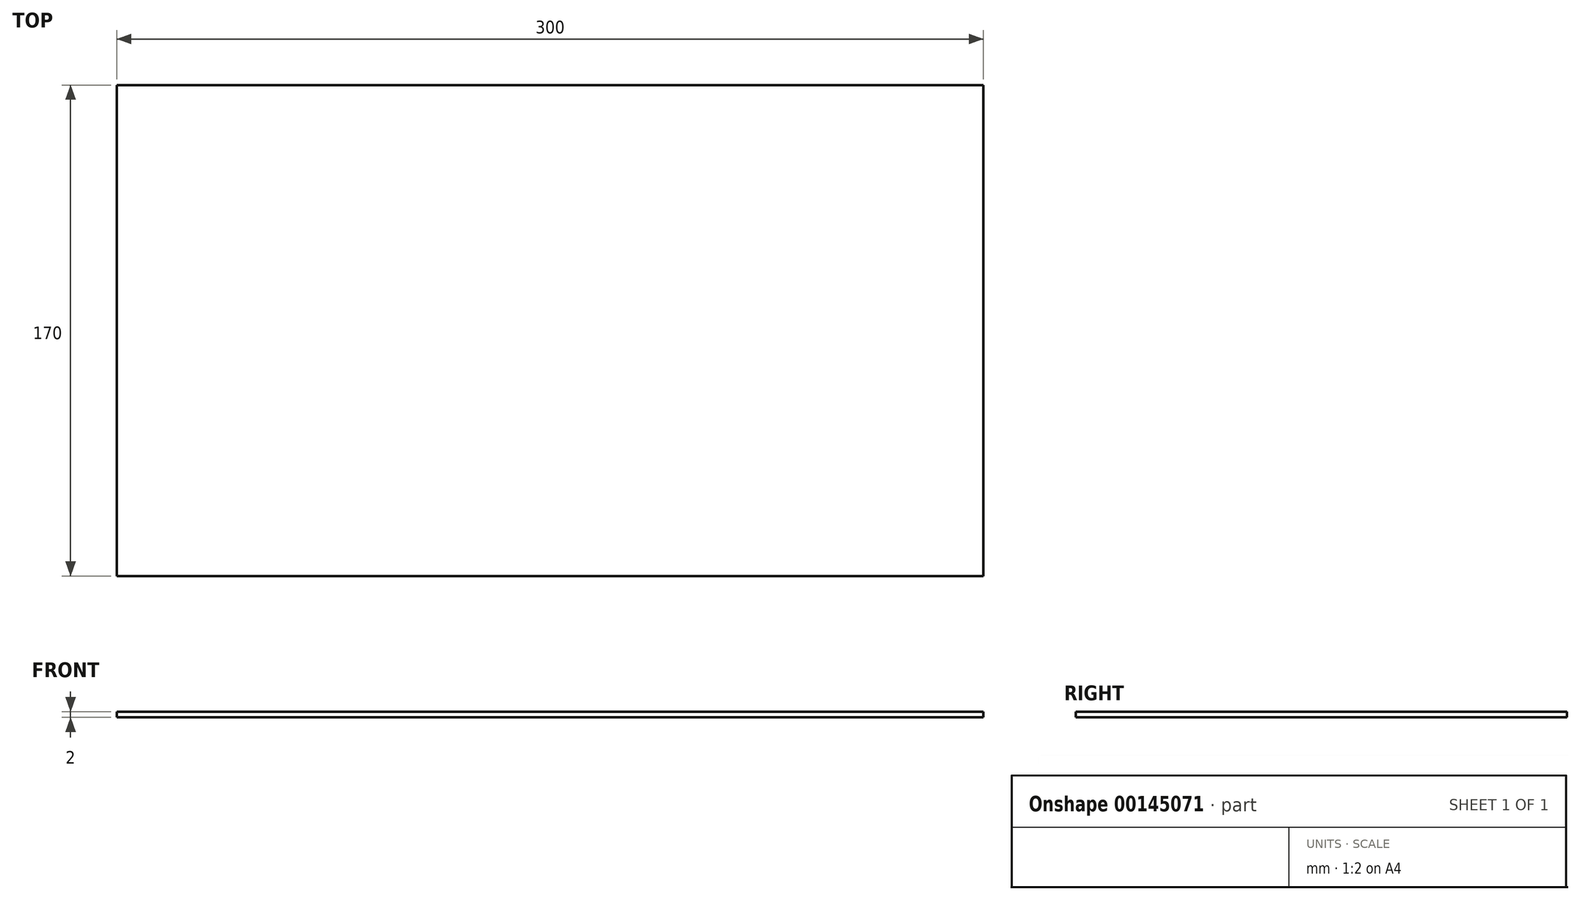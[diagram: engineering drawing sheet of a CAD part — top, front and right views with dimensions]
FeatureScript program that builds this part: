
annotation { "Feature Type Name" : "Feature", "Feature Type Description" : "" }
export const myFeature = defineFeature(function(context is Context, id is Id, definition is map)
    precondition{}
    {
        {
            var Q0;
            Q0=qCreatedBy(makeId("Top.planeOp"),FACE);
            var sketch = newSketch(context, id + "F0", { "sketchPlane" : qUnion([Q0])});
            skLineSegment(sketch, "E0.bottom", {"start": v(0, 0) * mm, "end": v(300, 0) * mm});
            skLineSegment(sketch, "E0.top", {"start": v(0, 170) * mm, "end": v(300, 170) * mm});
            skLineSegment(sketch, "E0.left", {"start": v(0, 0) * mm, "end": v(0, 170) * mm});
            skLineSegment(sketch, "E0.right", {"start": v(300, 0) * mm, "end": v(300, 170) * mm});
            skSolve(sketch);
        }
        {
            var Q0;
            Q0 = qSketchRegion(id + "F0", true);
            extrude(context, id + "F1", {"entities" : qUnion([Q0]), "depth" : 2 * mm});
        }
    });
